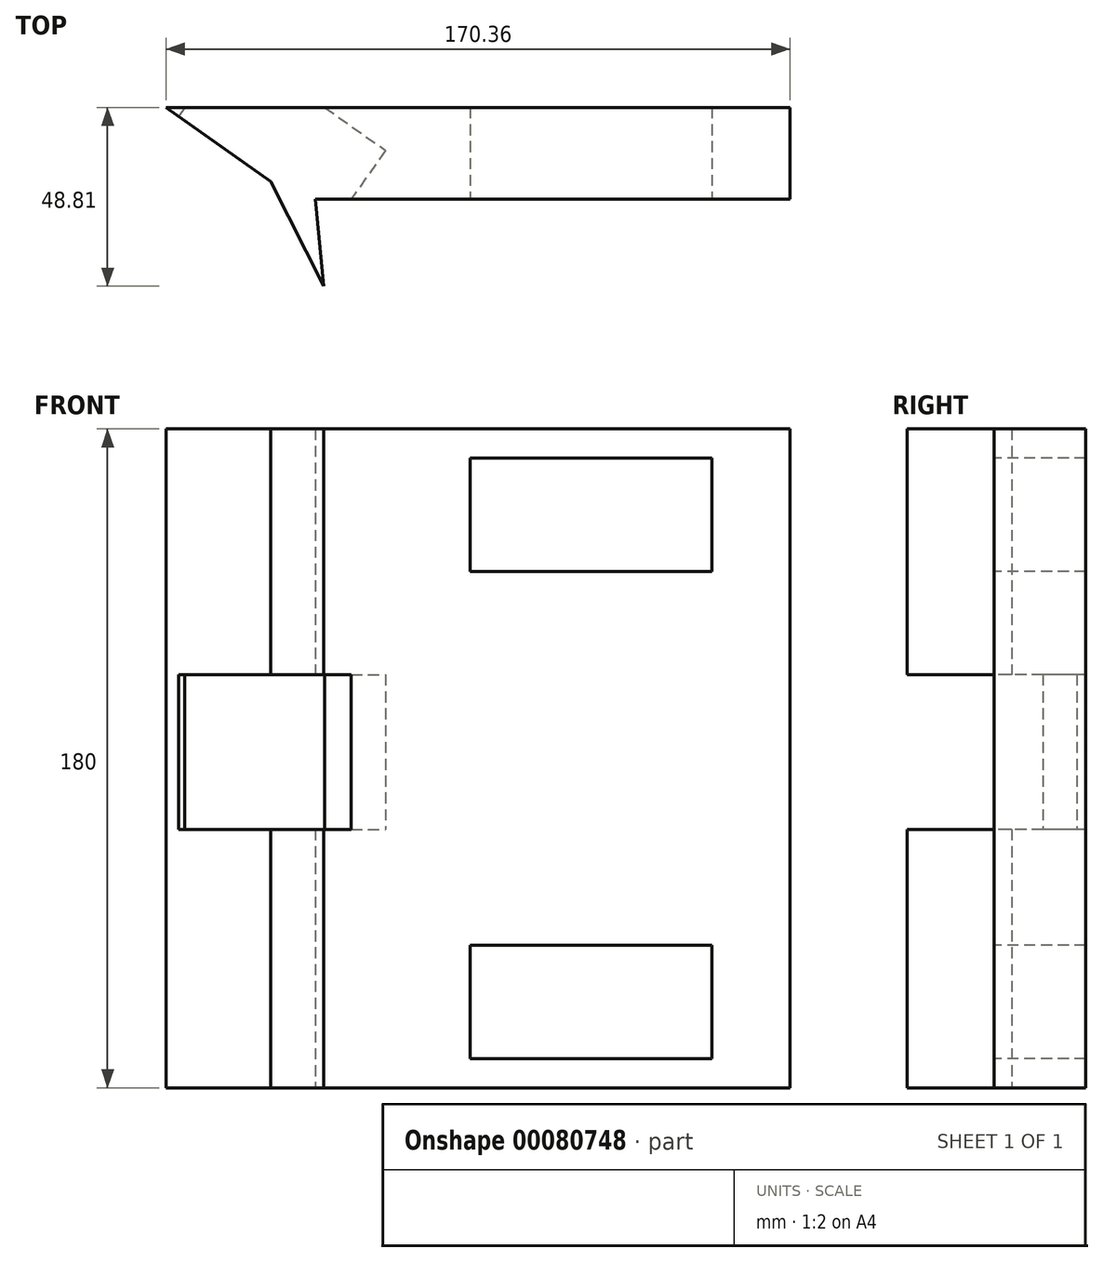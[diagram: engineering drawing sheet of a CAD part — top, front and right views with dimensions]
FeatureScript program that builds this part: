
annotation { "Feature Type Name" : "Feature", "Feature Type Description" : "" }
export const myFeature = defineFeature(function(context is Context, id is Id, definition is map)
    precondition{}
    {
        {
            var Q0;
            Q0=qCreatedBy(makeId("Front.planeOp"),FACE);
            var sketch = newSketch(context, id + "F0", { "sketchPlane" : qUnion([Q0])});
            skLineSegment(sketch, "E0.bottom", {"start": v(67.5, 90) * mm, "end": v(-67.5, 90) * mm});
            skLineSegment(sketch, "E0.top", {"start": v(67.5, -90) * mm, "end": v(-67.5, -90) * mm});
            skLineSegment(sketch, "E0.left", {"start": v(67.5, 90) * mm, "end": v(67.5, -90) * mm});
            skLineSegment(sketch, "E0.right", {"start": v(-67.5, 90) * mm, "end": v(-67.5, -90) * mm});
            skPoint(sketch, "E0.middle", {"position": v(0, 0) * mm});
            skLineSegment(sketch, "E1", {"start": v(0, 0) * mm, "end": v(0, 90) * mm, "construction": true});
            skSolve(sketch);
        }
        {
            var Q0;
            Q0=makeQuery(id+"F0.imprint","IMPRINT",FACE,{"disambiguationData":[TD([[makeQuery(id+"F0.imprint","IMPRINT",EDGE,{"derivedFrom":sQuery(id+"F0.wireOp",EDGE,"E0.bottom")}),1.0]])]});
            extrude(context, id + "F1", {"entities" : qUnion([Q0]), "depth" : 25 * mm});
        }
        {
            var Q0;
            Q0=makeQuery(id+"F1.opExtrude","SWEPT_FACE",FACE,{"disambiguationData":[OSD([sQuery(id+"F0.wireOp",EDGE,"E0.top")])]});
            var sketch = newSketch(context, id + "F2", { "sketchPlane" : qUnion([Q0])});
            skLineSegment(sketch, "E2", {"start": v(-67.5, 25) * mm, "end": v(-102.86, 0) * mm});
            skLineSegment(sketch, "E3", {"start": v(-102.86, 0) * mm, "end": v(-67.5, 0) * mm});
            skLineSegment(sketch, "E4", {"start": v(-67.5, 25) * mm, "end": v(-67.5, 0) * mm});
            skLineSegment(sketch, "E5", {"start": v(-67.5, 25) * mm, "end": v(-62.1, 25) * mm});
            skLineSegment(sketch, "E6", {"start": v(-59.83, 48.8) * mm, "end": v(-62.1, 25) * mm});
            skLineSegment(sketch, "E7", {"start": v(-59.83, 48.8) * mm, "end": v(-74.27, 20.21) * mm});
            skSolve(sketch);
        }
        {
            var Q0;
            Q0=makeQuery(id+"F2.imprint","IMPRINT",FACE,{"disambiguationData":[TD([[makeQuery(id+"F2.imprint","IMPRINT",EDGE,{"derivedFrom":sQuery(id+"F2.wireOp",EDGE,"5zBbHoMx-JPPf-hHJM-zQXc-xZs0RZ77oCch")}),-1.0]])]});
            var Q1;
            Q1=makeQuery(id+"F2.imprint","IMPRINT",FACE,{"disambiguationData":[TD([[makeQuery(id+"F2.imprint","IMPRINT",EDGE,{"derivedFrom":sQuery(id+"F2.wireOp",EDGE,"E5")}),-1.0]])]});
            var Q2;
            Q2=makeQuery(id+"F2.imprint","IMPRINT",FACE,{"disambiguationData":[TD([[makeQuery(id+"F2.imprint","IMPRINT",EDGE,{"derivedFrom":sQuery(id+"F2.wireOp",EDGE,"E2")}),1.0]])]});
            var Q3;
            Q3 = qSketchRegion(id + "F4", true);
            extrude(context, id + "F3", {"entities" : qUnion([Q0, Q1, Q2, Q3]), "operationType" : NewBodyOperationType.ADD, "oppositeDirection" : true, "depth" : 180 * mm});
        }
        {
            var Q0;
            Q0=makeQuery(id+"F3.opExtrude","SWEPT_FACE",FACE,{"disambiguationData":[OSD([sQuery(id+"F2.wireOp",EDGE,"E2")])]});
            var sketch = newSketch(context, id + "F4", { "sketchPlane" : qUnion([Q0])});
            skPoint(sketch, "E8.middle", {"position": v(-65.4, 0) * mm});
            skLineSegment(sketch, "E9.bottom", {"start": v(-79.86, 22.87) * mm, "end": v(-28.3, 22.87) * mm});
            skLineSegment(sketch, "E9.top", {"start": v(-79.86, -19.42) * mm, "end": v(-28.3, -19.42) * mm});
            skLineSegment(sketch, "E9.left", {"start": v(-79.86, 22.87) * mm, "end": v(-79.86, -19.42) * mm});
            skLineSegment(sketch, "E9.right", {"start": v(-28.3, 22.87) * mm, "end": v(-28.3, -19.42) * mm});
            skSolve(sketch);
        }
        {
            var Q0;
            Q0 = qSketchRegion(id + "F4", true);
            extrude(context, id + "F5", {"entities" : qUnion([Q0]), "operationType" : NewBodyOperationType.REMOVE, "oppositeDirection" : true, "depth" : 25 * mm});
        }
        {
            var Q0;
            Q0=makeQuery(id+"F1.opExtrude","CAP_FACE",FACE,{"disambiguationData":[OSD([sQuery(id+"F0.wireOp",EDGE,"E0.bottom"),sQuery(id+"F0.wireOp",EDGE,"E0.top"),sQuery(id+"F0.wireOp",EDGE,"E0.left"),sQuery(id+"F0.wireOp",EDGE,"E0.right")])],"isStart":false});
            var sketch = newSketch(context, id + "F6", { "sketchPlane" : qUnion([Q0])});
            skPoint(sketch, "E10.middle", {"position": v(-17.09, 0) * mm});
            skLineSegment(sketch, "E11.bottom", {"start": v(46.16, 82) * mm, "end": v(-19.88, 82) * mm});
            skLineSegment(sketch, "E11.top", {"start": v(46.16, 51) * mm, "end": v(-19.88, 51) * mm});
            skLineSegment(sketch, "E11.left", {"start": v(46.16, 82) * mm, "end": v(46.16, 51) * mm});
            skLineSegment(sketch, "E11.right", {"start": v(-19.88, 82) * mm, "end": v(-19.88, 51) * mm});
            skPoint(sketch, "E11.middle", {"position": v(13.14, 66.5) * mm});
            skLineSegment(sketch, "E12.bottom", {"start": v(46.16, -51) * mm, "end": v(-19.88, -51) * mm});
            skLineSegment(sketch, "E12.top", {"start": v(46.16, -82) * mm, "end": v(-19.88, -82) * mm});
            skLineSegment(sketch, "E12.left", {"start": v(46.16, -51) * mm, "end": v(46.16, -82) * mm});
            skLineSegment(sketch, "E12.right", {"start": v(-19.88, -51) * mm, "end": v(-19.88, -82) * mm});
            skPoint(sketch, "E12.middle", {"position": v(13.14, -66.5) * mm});
            skSolve(sketch);
        }
        {
            var Q0;
            Q0=makeQuery(id+"F6.imprint","IMPRINT",FACE,{"disambiguationData":[TD([[makeQuery(id+"F6.imprint","IMPRINT",EDGE,{"derivedFrom":sQuery(id+"F6.wireOp",EDGE,"E10.bottom")}),1.0]])]});
            var Q1;
            Q1=makeQuery(id+"F6.imprint","IMPRINT",FACE,{"disambiguationData":[TD([[makeQuery(id+"F6.imprint","IMPRINT",EDGE,{"derivedFrom":sQuery(id+"F6.wireOp",EDGE,"E11.bottom")}),1.0]])]});
            var Q2;
            Q2=makeQuery(id+"F6.imprint","IMPRINT",FACE,{"disambiguationData":[TD([[makeQuery(id+"F6.imprint","IMPRINT",EDGE,{"derivedFrom":sQuery(id+"F6.wireOp",EDGE,"E12.bottom")}),1.0]])]});
            extrude(context, id + "F7", {"entities" : qUnion([Q0, Q1, Q2]), "operationType" : NewBodyOperationType.REMOVE, "oppositeDirection" : true, "depth" : 25 * mm});
        }
        {
            var Q0;
            Q0=makeQuery(id+"F3.opExtrude","SWEPT_FACE",FACE,{"disambiguationData":[OSD([sQuery(id+"F2.wireOp",EDGE,"E7")])]});
            var sketch = newSketch(context, id + "F8", { "sketchPlane" : qUnion([Q0])});
            skLineSegment(sketch, "E13.bottom", {"start": v(-15.43, 22.87) * mm, "end": v(16.6, 22.87) * mm});
            skLineSegment(sketch, "E13.top", {"start": v(-15.43, -19.42) * mm, "end": v(16.6, -19.42) * mm});
            skLineSegment(sketch, "E13.left", {"start": v(-15.43, 22.87) * mm, "end": v(-15.43, -19.42) * mm});
            skLineSegment(sketch, "E13.right", {"start": v(16.6, 22.87) * mm, "end": v(16.6, -19.42) * mm});
            skSolve(sketch);
        }
        {
            var Q0;
            Q0=makeQuery(id+"F8.imprint","IMPRINT",FACE,{"disambiguationData":[TD([[makeQuery(id+"F8.imprint","IMPRINT",EDGE,{"derivedFrom":sQuery(id+"F8.wireOp",EDGE,"E13.bottom")}),-1.0]])]});
            extrude(context, id + "F9", {"entities" : qUnion([Q0]), "operationType" : NewBodyOperationType.REMOVE, "oppositeDirection" : true, "depth" : 10 * mm});
        }
    });
